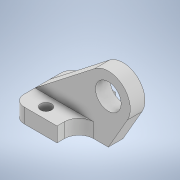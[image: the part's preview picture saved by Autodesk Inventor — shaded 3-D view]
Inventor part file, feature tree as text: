
AUTODESK INVENTOR PART (.ipt)
format: ipt  version: 2022.2 (Build 262287030, 287C)  size: 148,480 bytes
history: native  units: in
note: dims shown in document units (in); Inventor stores cm internally (conversion verified against a paired STEP export)
features: extrude x2, sketch x2
ambient origin geometry x8: Origin, YZ Plane, XZ Plane, XY Plane, X Axis, Y Axis, Z Axis, Center Point
bodies: Solid1 (feature_tree)
feature tree (4):
  extrude  "Extrusion1"  Depth=1.5in
  extrude  "Extrusion2"  Depth=1.0in
  sketch  "Sketch1"  dims[d0=1.75in d1=1.5in]
  sketch  "Sketch2"  dims[d2=3.0in d3=5.0in d4=1.0in d5=1.0in d6=0.0in d7=0.75in d8=4.0in d9=0.75in d10=3.0in d11=1.0in d12=0.75in d13=1.5in d14=1.0in d15=0.0in]
